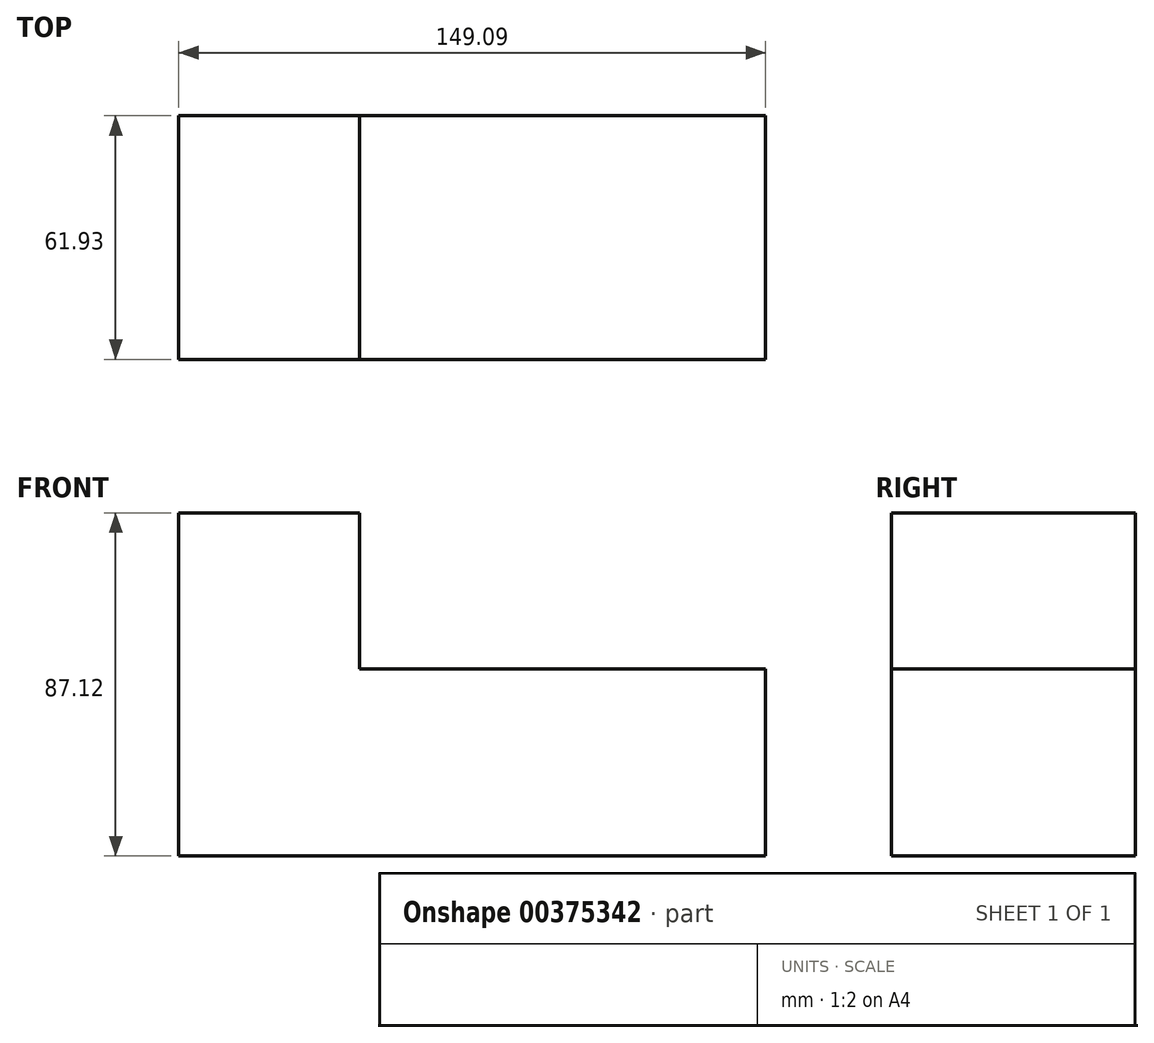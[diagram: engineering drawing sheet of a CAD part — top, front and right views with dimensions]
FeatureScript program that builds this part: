
annotation { "Feature Type Name" : "Feature", "Feature Type Description" : "" }
export const myFeature = defineFeature(function(context is Context, id is Id, definition is map)
    precondition{}
    {
        {
            var Q0;
            Q0=qCreatedBy(makeId("Front.planeOp"),FACE);
            var sketch = newSketch(context, id + "F0", { "sketchPlane" : qUnion([Q0])});
            skLineSegment(sketch, "E0", {"start": v(-61.62, 39.62) * mm, "end": v(-61.62, -47.5) * mm});
            skLineSegment(sketch, "E1", {"start": v(-61.62, -47.5) * mm, "end": v(87.47, -47.5) * mm});
            skLineSegment(sketch, "E2", {"start": v(87.47, -47.5) * mm, "end": v(87.47, 0) * mm});
            skLineSegment(sketch, "E3", {"start": v(-61.62, 39.62) * mm, "end": v(-15.65, 39.62) * mm});
            skLineSegment(sketch, "E4", {"start": v(-15.65, 39.62) * mm, "end": v(-15.65, 0) * mm});
            skLineSegment(sketch, "E5", {"start": v(-15.65, 0) * mm, "end": v(87.47, 0) * mm});
            skSolve(sketch);
        }
        {
            var Q0;
            Q0=makeQuery(id+"F0.imprint","IMPRINT",FACE,{"disambiguationData":[TD([[makeQuery(id+"F0.imprint","IMPRINT",EDGE,{"derivedFrom":sQuery(id+"F0.wireOp",EDGE,"E0")}),1.0]])]});
            extrude(context, id + "F1", {"entities" : qUnion([Q0]), "depth" : 25.4 * mm, "hasSecondDirection" : true, "secondDirectionOppositeDirection" : true, "secondDirectionDepth" : 36.53 * mm});
        }
    });
